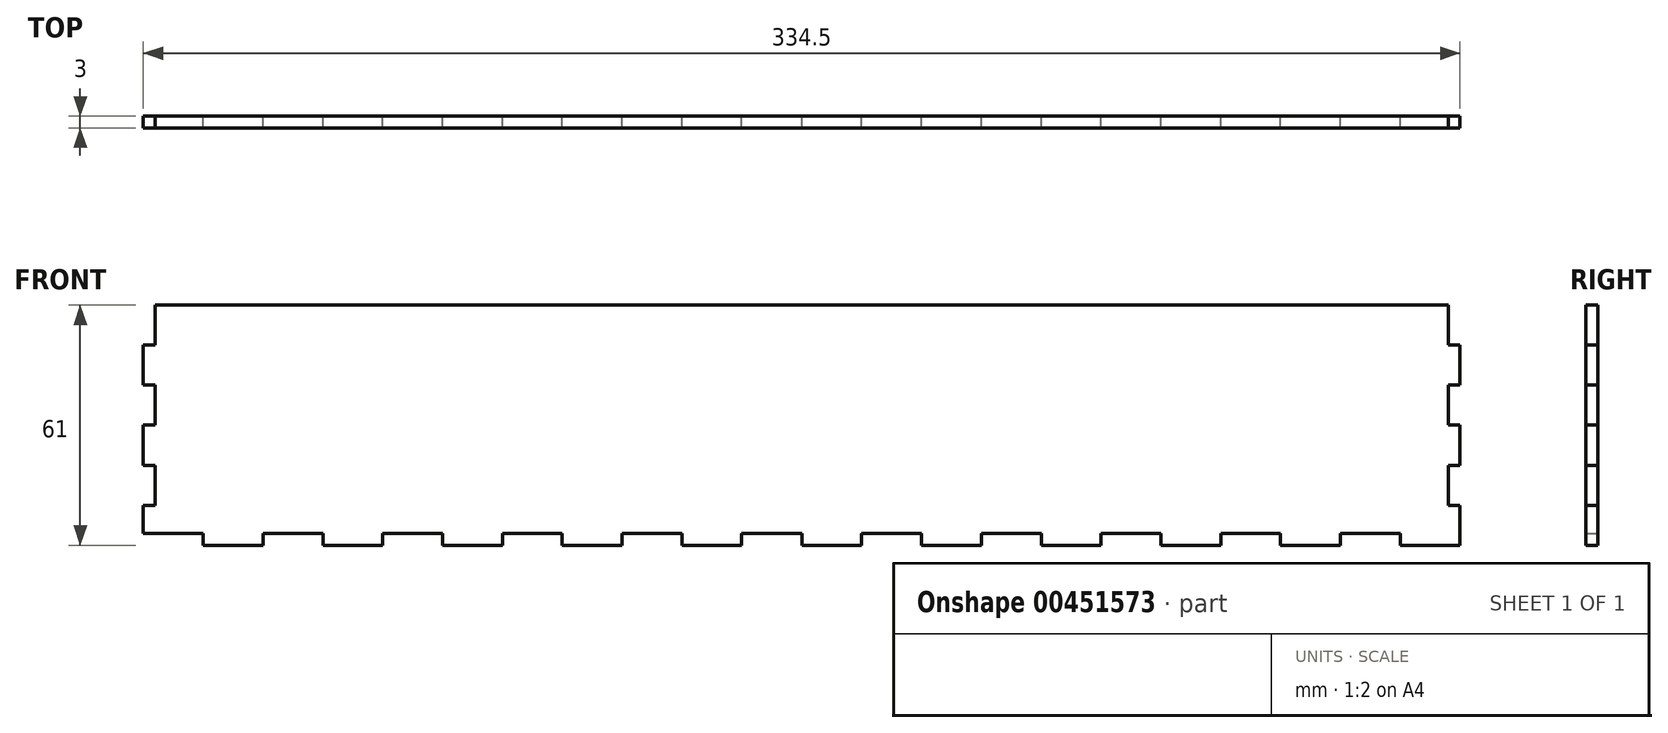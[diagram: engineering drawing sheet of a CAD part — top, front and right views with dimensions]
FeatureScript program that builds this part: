
annotation { "Feature Type Name" : "Feature", "Feature Type Description" : "" }
export const myFeature = defineFeature(function(context is Context, id is Id, definition is map)
    precondition{}
    {
        {
            var Q0;
            Q0=qCreatedBy(makeId("Front.planeOp"),FACE);
            var sketch = newSketch(context, id + "F0", { "sketchPlane" : qUnion([Q0])});
            skLineSegment(sketch, "E0.bottom", {"start": v(167.25, -30.5) * mm, "end": v(152.05, -30.5) * mm});
            skLineSegment(sketch, "E0.top", {"start": v(164.25, 30.5) * mm, "end": v(-164.25, 30.5) * mm});
            skLineSegment(sketch, "E0.left", {"start": v(167.25, -30.5) * mm, "end": v(167.25, -20.33) * mm});
            skLineSegment(sketch, "E0.right", {"start": v(-167.25, -27.5) * mm, "end": v(-167.25, -20.33) * mm});
            skPoint(sketch, "E0.middle", {"position": v(0, 0) * mm});
            skLineSegment(sketch, "E1", {"start": v(-167.25, -27.5) * mm, "end": v(-152.05, -27.5) * mm});
            skLineSegment(sketch, "E2", {"start": v(-152.05, -27.5) * mm, "end": v(-152.05, -30.5) * mm});
            skLineSegment(sketch, "E3", {"start": v(-136.85, -27.5) * mm, "end": v(-136.85, -30.5) * mm});
            skLineSegment(sketch, "E4", {"start": v(-121.65, -27.5) * mm, "end": v(-121.65, -30.5) * mm});
            skLineSegment(sketch, "E5", {"start": v(-106.45, -27.5) * mm, "end": v(-106.45, -30.5) * mm});
            skLineSegment(sketch, "E6", {"start": v(-91.25, -27.5) * mm, "end": v(-91.25, -30.5) * mm});
            skLineSegment(sketch, "E7", {"start": v(-76.05, -27.5) * mm, "end": v(-76.05, -30.5) * mm});
            skLineSegment(sketch, "E8", {"start": v(-60.85, -27.5) * mm, "end": v(-60.85, -30.5) * mm});
            skLineSegment(sketch, "E9", {"start": v(-45.65, -27.5) * mm, "end": v(-45.65, -30.5) * mm});
            skLineSegment(sketch, "E10", {"start": v(-30.45, -27.5) * mm, "end": v(-30.45, -30.5) * mm});
            skLineSegment(sketch, "E11", {"start": v(-15.25, -27.5) * mm, "end": v(-15.25, -30.5) * mm});
            skLineSegment(sketch, "E12", {"start": v(-0.05, -30.5) * mm, "end": v(-0.05, -27.5) * mm});
            skLineSegment(sketch, "E13.MirrorCS", {"start": v(45.65, -27.5) * mm, "end": v(45.65, -30.5) * mm});
            skLineSegment(sketch, "E14.MirrorCS", {"start": v(60.85, -27.5) * mm, "end": v(60.85, -30.5) * mm});
            skLineSegment(sketch, "E15.MirrorCS", {"start": v(30.45, -27.5) * mm, "end": v(30.45, -30.5) * mm});
            skLineSegment(sketch, "E16.MirrorCS", {"start": v(76.05, -27.5) * mm, "end": v(76.05, -30.5) * mm});
            skLineSegment(sketch, "E17.MirrorCS", {"start": v(106.45, -27.5) * mm, "end": v(106.45, -30.5) * mm});
            skLineSegment(sketch, "E18.MirrorCS", {"start": v(121.65, -27.5) * mm, "end": v(121.65, -30.5) * mm});
            skLineSegment(sketch, "E19.MirrorCS", {"start": v(136.85, -27.5) * mm, "end": v(136.85, -30.5) * mm});
            skLineSegment(sketch, "E20.MirrorCS", {"start": v(15.25, -27.5) * mm, "end": v(15.25, -30.5) * mm});
            skLineSegment(sketch, "E21.MirrorCS", {"start": v(91.25, -27.5) * mm, "end": v(91.25, -30.5) * mm});
            skLineSegment(sketch, "E22.MirrorCS", {"start": v(0.05, -30.5) * mm, "end": v(0.05, -27.5) * mm});
            skLineSegment(sketch, "E23.MirrorCS", {"start": v(152.05, -27.5) * mm, "end": v(152.05, -30.5) * mm});
            skPoint(sketch, "E24.orphan", {"position": v(-167.25, -30.5) * mm});
            skLineSegment(sketch, "E25.trimOffspring", {"start": v(-136.85, -27.5) * mm, "end": v(-121.65, -27.5) * mm});
            skLineSegment(sketch, "E26.trimOffspring", {"start": v(-136.85, -30.5) * mm, "end": v(-152.05, -30.5) * mm});
            skLineSegment(sketch, "E27.trimOffspring", {"start": v(-106.45, -27.5) * mm, "end": v(-91.25, -27.5) * mm});
            skLineSegment(sketch, "E28.trimOffspring", {"start": v(-106.45, -30.5) * mm, "end": v(-121.65, -30.5) * mm});
            skLineSegment(sketch, "E29.trimOffspring", {"start": v(-76.05, -27.5) * mm, "end": v(-60.85, -27.5) * mm});
            skLineSegment(sketch, "E30.trimOffspring", {"start": v(-76.05, -30.5) * mm, "end": v(-91.25, -30.5) * mm});
            skLineSegment(sketch, "E31.trimOffspring", {"start": v(-45.65, -27.5) * mm, "end": v(-30.45, -27.5) * mm});
            skLineSegment(sketch, "E32.trimOffspring", {"start": v(-45.65, -30.5) * mm, "end": v(-60.85, -30.5) * mm});
            skLineSegment(sketch, "E33.trimOffspring", {"start": v(-15.25, -27.5) * mm, "end": v(0.05, -27.5) * mm});
            skLineSegment(sketch, "E34.trimOffspring", {"start": v(-15.25, -30.5) * mm, "end": v(-30.45, -30.5) * mm});
            skLineSegment(sketch, "E35.trimOffspring", {"start": v(15.25, -27.5) * mm, "end": v(30.45, -27.5) * mm});
            skLineSegment(sketch, "E36.trimOffspring", {"start": v(15.25, -30.5) * mm, "end": v(-0.05, -30.5) * mm});
            skLineSegment(sketch, "E37.trimOffspring", {"start": v(45.65, -27.5) * mm, "end": v(60.85, -27.5) * mm});
            skLineSegment(sketch, "E38.trimOffspring", {"start": v(45.65, -30.5) * mm, "end": v(30.45, -30.5) * mm});
            skLineSegment(sketch, "E39.trimOffspring", {"start": v(76.05, -27.5) * mm, "end": v(91.25, -27.5) * mm});
            skLineSegment(sketch, "E40.trimOffspring", {"start": v(76.05, -30.5) * mm, "end": v(60.85, -30.5) * mm});
            skLineSegment(sketch, "E41.trimOffspring", {"start": v(106.45, -27.5) * mm, "end": v(121.65, -27.5) * mm});
            skLineSegment(sketch, "E42.trimOffspring", {"start": v(106.45, -30.5) * mm, "end": v(91.25, -30.5) * mm});
            skLineSegment(sketch, "E43.trimOffspring", {"start": v(136.85, -27.5) * mm, "end": v(152.05, -27.5) * mm});
            skLineSegment(sketch, "E44.trimOffspring", {"start": v(136.85, -30.5) * mm, "end": v(121.65, -30.5) * mm});
            skLineSegment(sketch, "E45", {"start": v(-164.25, 30.5) * mm, "end": v(-164.25, 20.33) * mm});
            skLineSegment(sketch, "E46", {"start": v(-167.25, 20.33) * mm, "end": v(-164.25, 20.33) * mm});
            skLineSegment(sketch, "E47", {"start": v(-167.25, 10.17) * mm, "end": v(-164.25, 10.17) * mm});
            skLineSegment(sketch, "E48", {"start": v(-167.25, 0) * mm, "end": v(-164.25, 0) * mm});
            skLineSegment(sketch, "E49", {"start": v(-167.25, -10.16) * mm, "end": v(-164.25, -10.16) * mm});
            skLineSegment(sketch, "E50", {"start": v(-167.25, -20.33) * mm, "end": v(-164.25, -20.33) * mm});
            skPoint(sketch, "E51.orphan", {"position": v(-167.25, 30.5) * mm});
            skLineSegment(sketch, "E52.trimOffspring", {"start": v(-164.25, 10.17) * mm, "end": v(-164.25, 0) * mm});
            skLineSegment(sketch, "E53.trimOffspring", {"start": v(-167.25, 10.17) * mm, "end": v(-167.25, 20.33) * mm});
            skLineSegment(sketch, "E54.trimOffspring", {"start": v(-164.25, -10.16) * mm, "end": v(-164.25, -20.33) * mm});
            skLineSegment(sketch, "E55.trimOffspring", {"start": v(-167.25, -10.16) * mm, "end": v(-167.25, 0) * mm});
            skLineSegment(sketch, "E56.MirrorCS", {"start": v(167.25, 0) * mm, "end": v(164.25, 0) * mm});
            skLineSegment(sketch, "E57.MirrorCS", {"start": v(167.25, -10.16) * mm, "end": v(164.25, -10.16) * mm});
            skLineSegment(sketch, "E58.MirrorCS", {"start": v(167.25, -20.33) * mm, "end": v(164.25, -20.33) * mm});
            skLineSegment(sketch, "E59.MirrorCS", {"start": v(167.25, 10.17) * mm, "end": v(164.25, 10.17) * mm});
            skLineSegment(sketch, "E60.MirrorCS", {"start": v(167.25, 20.33) * mm, "end": v(164.25, 20.33) * mm});
            skLineSegment(sketch, "E61.MirrorCS", {"start": v(167.25, 10.17) * mm, "end": v(167.25, 20.33) * mm});
            skLineSegment(sketch, "E62.MirrorCS", {"start": v(164.25, 30.5) * mm, "end": v(164.25, 20.33) * mm});
            skPoint(sketch, "E63.MirrorP", {"position": v(167.25, 30.5) * mm});
            skLineSegment(sketch, "E64.MirrorCS", {"start": v(167.25, -27.5) * mm, "end": v(167.25, -20.33) * mm});
            skLineSegment(sketch, "E65.MirrorCS", {"start": v(164.25, -10.16) * mm, "end": v(164.25, -20.33) * mm});
            skLineSegment(sketch, "E66.MirrorCS", {"start": v(167.25, -10.16) * mm, "end": v(167.25, 0) * mm});
            skLineSegment(sketch, "E67.MirrorCS", {"start": v(164.25, 10.17) * mm, "end": v(164.25, 0) * mm});
            skSolve(sketch);
        }
        {
            var Q0;
            Q0=makeQuery(id+"F0.imprint","IMPRINT",FACE,{"disambiguationData":[TD([[makeQuery(id+"F0.imprint","IMPRINT",EDGE,{"derivedFrom":sQuery(id+"F0.wireOp",EDGE,"E0.bottom")}),-1.0]])]});
            extrude(context, id + "F1", {"entities" : qUnion([Q0]), "depth" : 3 * mm, "offsetDistance" : 25 * mm});
        }
    });
